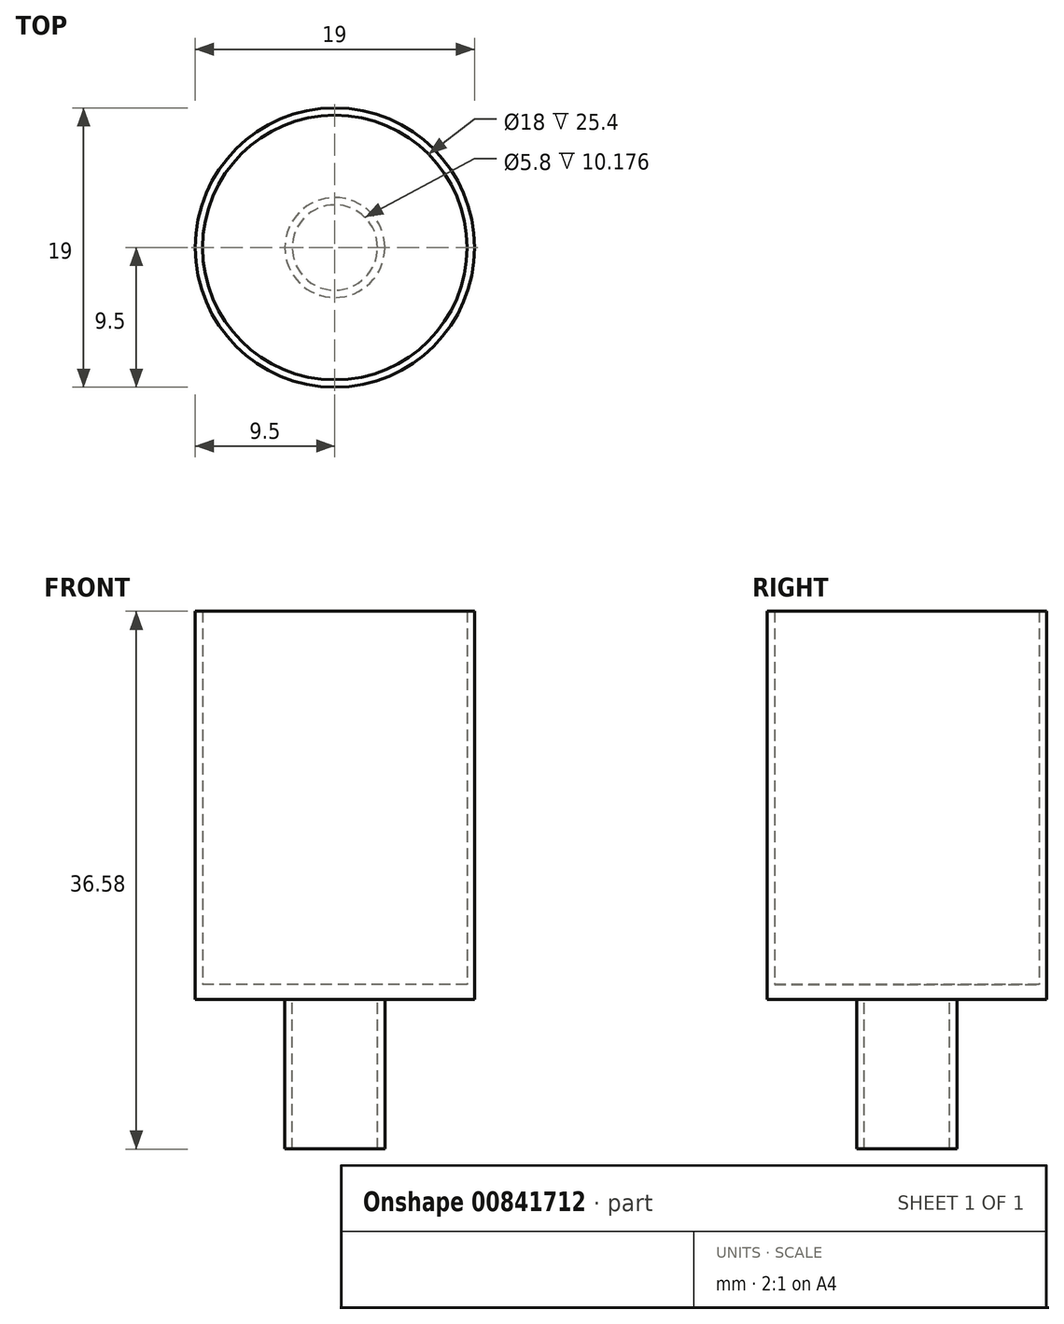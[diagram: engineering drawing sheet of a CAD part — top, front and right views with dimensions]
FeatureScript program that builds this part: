
annotation { "Feature Type Name" : "Feature", "Feature Type Description" : "" }
export const myFeature = defineFeature(function(context is Context, id is Id, definition is map)
    precondition{}
    {
        {
            var Q0;
            Q0=qCreatedBy(makeId("Top.planeOp"),FACE);
            var sketch = newSketch(context, id + "F0", { "sketchPlane" : qUnion([Q0])});
            skCircle(sketch, "E0", {"center": v(0, 0) * mm, "radius": 9.5 * mm});
            skCircle(sketch, "E1", {"center": v(0, 0) * mm, "radius": 9 * mm});
            skCircle(sketch, "E2", {"center": v(0, 0) * mm, "radius": 3.4 * mm});
            skCircle(sketch, "E3", {"center": v(0, 0) * mm, "radius": 2.9 * mm});
            skSolve(sketch);
        }
        {
            var Q0;
            Q0=makeQuery(id+"F0.imprint","IMPRINT",FACE,{"disambiguationData":[TD([[makeQuery(id+"F0.imprint","IMPRINT",EDGE,{"derivedFrom":sQuery(id+"F0.wireOp",EDGE,"E0")}),1.0]])]});
            extrude(context, id + "F1", {"entities" : qUnion([Q0]), "depth" : 25.4 * mm, "offsetDistance" : 25.4 * mm});
        }
        {
            var Q0;
            Q0=makeQuery(id+"F0.imprint","IMPRINT",FACE,{"disambiguationData":[TD([[makeQuery(id+"F0.imprint","IMPRINT",EDGE,{"derivedFrom":sQuery(id+"F0.wireOp",EDGE,"E0")}),1.0]])]});
            var Q1;
            Q1=makeQuery(id+"F0.imprint","IMPRINT",FACE,{"disambiguationData":[TD([[makeQuery(id+"F0.imprint","IMPRINT",EDGE,{"derivedFrom":sQuery(id+"F0.wireOp",EDGE,"E1")}),1.0]])]});
            var Q2;
            Q2=makeQuery(id+"F0.imprint","IMPRINT",FACE,{"disambiguationData":[TD([[makeQuery(id+"F0.imprint","IMPRINT",EDGE,{"derivedFrom":sQuery(id+"F0.wireOp",EDGE,"E3")}),1.0]])]});
            var Q3;
            Q3=makeQuery(id+"F0.imprint","IMPRINT",FACE,{"disambiguationData":[TD([[makeQuery(id+"F0.imprint","IMPRINT",EDGE,{"derivedFrom":sQuery(id+"F0.wireOp",EDGE,"E2")}),1.0]])]});
            extrude(context, id + "F2", {"entities" : qUnion([Q0, Q1, Q2, Q3]), "operationType" : NewBodyOperationType.ADD, "oppositeDirection" : true, "depth" : 1 * mm, "offsetDistance" : 25.4 * mm});
        }
        {
            var Q0;
            Q0=makeQuery(id+"F0.imprint","IMPRINT",FACE,{"disambiguationData":[TD([[makeQuery(id+"F0.imprint","IMPRINT",EDGE,{"derivedFrom":sQuery(id+"F0.wireOp",EDGE,"E2")}),1.0]])]});
            extrude(context, id + "F3", {"entities" : qUnion([Q0]), "operationType" : NewBodyOperationType.ADD, "oppositeDirection" : true, "depth" : 11.18 * mm, "offsetDistance" : 25.4 * mm});
        }
    });
